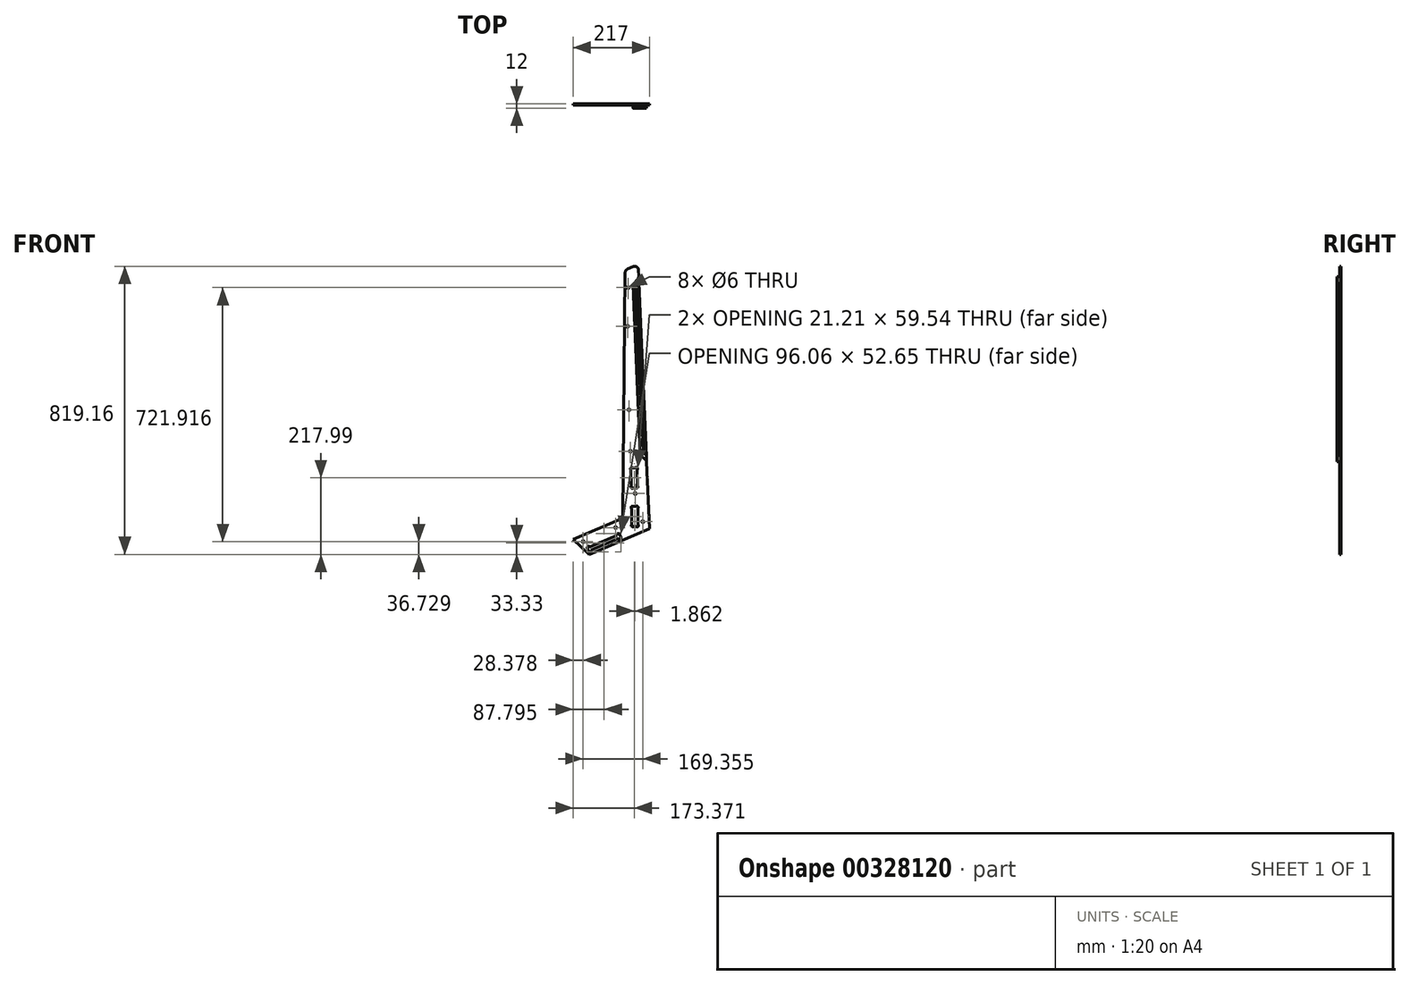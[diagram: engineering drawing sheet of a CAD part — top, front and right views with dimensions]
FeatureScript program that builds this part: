
annotation { "Feature Type Name" : "Feature", "Feature Type Description" : "" }
export const myFeature = defineFeature(function(context is Context, id is Id, definition is map)
    precondition{}
    {
        {
            var Q0;
            Q0=qCreatedBy(makeId("Front.planeOp"),FACE);
            var sketch = newSketch(context, id + "F0", { "sketchPlane" : qUnion([Q0])});
            skArc(sketch, "E0", {"start": v(65.23, -72.8) * mm, "mid": v(65.32, -78.46) * mm, "end": v(70.98, -78.36) * mm});
            skLineSegment(sketch, "E1", {"start": v(70.98, -78.36) * mm, "end": v(77.67, -78.25) * mm});
            skArc(sketch, "E2", {"start": v(77.67, -78.25) * mm, "mid": v(83.32, -78.15) * mm, "end": v(83.23, -72.5) * mm});
            skLineSegment(sketch, "E3", {"start": v(83.23, -72.5) * mm, "end": v(82.45, -26.82) * mm});
            skArc(sketch, "E4", {"start": v(82.45, -26.82) * mm, "mid": v(82.36, -21.16) * mm, "end": v(76.7, -21.26) * mm});
            skLineSegment(sketch, "E5", {"start": v(76.7, -21.26) * mm, "end": v(70.02, -21.37) * mm});
            skArc(sketch, "E6", {"start": v(70.02, -21.37) * mm, "mid": v(64.36, -21.47) * mm, "end": v(64.46, -27.12) * mm});
            skLineSegment(sketch, "E7", {"start": v(64.46, -27.12) * mm, "end": v(65.23, -72.8) * mm});
            skLineSegment(sketch, "E8", {"start": v(85.09, -182.48) * mm, "end": v(84.31, -136.8) * mm});
            skArc(sketch, "E9", {"start": v(84.31, -136.8) * mm, "mid": v(84.22, -131.15) * mm, "end": v(78.56, -131.24) * mm});
            skLineSegment(sketch, "E10", {"start": v(78.56, -131.24) * mm, "end": v(71.88, -131.35) * mm});
            skArc(sketch, "E11", {"start": v(71.88, -131.35) * mm, "mid": v(66.22, -131.45) * mm, "end": v(66.32, -137.1) * mm});
            skLineSegment(sketch, "E12", {"start": v(66.32, -137.1) * mm, "end": v(67.09, -182.79) * mm});
            skArc(sketch, "E13", {"start": v(67.09, -182.79) * mm, "mid": v(67.19, -188.44) * mm, "end": v(72.84, -188.35) * mm});
            skLineSegment(sketch, "E14", {"start": v(72.84, -188.35) * mm, "end": v(79.53, -188.23) * mm});
            skArc(sketch, "E15", {"start": v(79.53, -188.23) * mm, "mid": v(85.18, -188.14) * mm, "end": v(85.09, -182.48) * mm});
            skArc(sketch, "E16", {"start": v(-52.1, -246.94) * mm, "mid": v(-57.35, -244.85) * mm, "end": v(-59.44, -250.1) * mm});
            skLineSegment(sketch, "E17", {"start": v(-59.44, -250.1) * mm, "end": v(-55.88, -258.37) * mm});
            skArc(sketch, "E18", {"start": v(-55.88, -258.37) * mm, "mid": v(-50.62, -260.47) * mm, "end": v(-48.53, -255.21) * mm});
            skLineSegment(sketch, "E19", {"start": v(-48.53, -255.21) * mm, "end": v(28.62, -222) * mm});
            skArc(sketch, "E20", {"start": v(28.62, -222) * mm, "mid": v(33.88, -224.09) * mm, "end": v(35.97, -218.83) * mm});
            skLineSegment(sketch, "E21", {"start": v(35.97, -218.83) * mm, "end": v(32.41, -210.57) * mm});
            skArc(sketch, "E22", {"start": v(32.41, -210.57) * mm, "mid": v(27.15, -208.47) * mm, "end": v(25.06, -213.73) * mm});
            skLineSegment(sketch, "E23", {"start": v(25.06, -213.73) * mm, "end": v(-52.1, -246.94) * mm});
            skArc(sketch, "E24", {"start": v(41.94, -161.76) * mm, "mid": v(41.27, -163.94) * mm, "end": v(39.52, -165.4) * mm});
            skLineSegment(sketch, "E25", {"start": v(39.52, -165.4) * mm, "end": v(-99.53, -225.26) * mm});
            skLineSegment(sketch, "E26", {"start": v(-99.53, -225.26) * mm, "end": v(-53.74, -267.8) * mm});
            skLineSegment(sketch, "E27", {"start": v(-53.74, -267.8) * mm, "end": v(41.34, -226.86) * mm});
            skLineSegment(sketch, "E28", {"start": v(41.34, -226.86) * mm, "end": v(117.47, -194.09) * mm});
            skLineSegment(sketch, "E29", {"start": v(117.47, -194.09) * mm, "end": v(85.73, 541.79) * mm});
            skArc(sketch, "E30", {"start": v(85.73, 541.79) * mm, "mid": v(81.05, 549.82) * mm, "end": v(71.78, 550.54) * mm});
            skLineSegment(sketch, "E31", {"start": v(71.78, 550.54) * mm, "end": v(54.43, 543.07) * mm});
            skArc(sketch, "E32", {"start": v(54.43, 543.07) * mm, "mid": v(50.05, 539.42) * mm, "end": v(48.38, 533.98) * mm});
            skLineSegment(sketch, "E33", {"start": v(48.38, 533.98) * mm, "end": v(41.94, -161.76) * mm});
            skCircle(sketch, "E34", {"center": v(56.39, 490.84) * mm, "radius": 3 * mm});
            skCircle(sketch, "E35", {"center": v(55.37, 380.85) * mm, "radius": 3 * mm});
            skCircle(sketch, "E36", {"center": v(-71.15, -231.07) * mm, "radius": 3 * mm});
            skCircle(sketch, "E37", {"center": v(76.63, -94.57) * mm, "radius": 3 * mm});
            skCircle(sketch, "E38", {"center": v(21.3, -191.27) * mm, "radius": 3 * mm});
            skCircle(sketch, "E39", {"center": v(63.23, 25.56) * mm, "radius": 3 * mm});
            skCircle(sketch, "E40", {"center": v(59.35, 143.54) * mm, "radius": 3 * mm});
            skCircle(sketch, "E41", {"center": v(98.2, -174.5) * mm, "radius": 3 * mm});
            skLineSegment(sketch, "E42", {"start": v(96.02, 524.96) * mm, "end": v(118.95, -6.55) * mm});
            skArc(sketch, "E43", {"start": v(118.95, -6.55) * mm, "mid": v(114.38, -11.53) * mm, "end": v(109.4, -6.96) * mm});
            skLineSegment(sketch, "E44", {"start": v(109.4, -6.96) * mm, "end": v(109.28, -4.28) * mm});
            skArc(sketch, "E45", {"start": v(109.28, -4.28) * mm, "mid": v(108.54, -1.25) * mm, "end": v(106.7, 1.27) * mm});
            skLineSegment(sketch, "E46", {"start": v(106.7, 1.27) * mm, "end": v(92.42, 14.37) * mm});
            skArc(sketch, "E47", {"start": v(92.42, 14.37) * mm, "mid": v(91.5, 15.63) * mm, "end": v(91.13, 17.14) * mm});
            skLineSegment(sketch, "E48", {"start": v(91.13, 17.14) * mm, "end": v(70.34, 498.96) * mm});
            skArc(sketch, "E49", {"start": v(70.34, 498.96) * mm, "mid": v(70.58, 500.5) * mm, "end": v(71.4, 501.83) * mm});
            skLineSegment(sketch, "E50", {"start": v(71.4, 501.83) * mm, "end": v(84.49, 516.1) * mm});
            skArc(sketch, "E51", {"start": v(84.49, 516.1) * mm, "mid": v(86.11, 518.78) * mm, "end": v(86.59, 521.86) * mm});
            skLineSegment(sketch, "E52", {"start": v(86.59, 521.86) * mm, "end": v(86.47, 524.54) * mm});
            skArc(sketch, "E53", {"start": v(86.47, 524.54) * mm, "mid": v(91.04, 529.53) * mm, "end": v(96.02, 524.96) * mm});
            skArc(sketch, "E54", {"start": v(99.45, 23.9) * mm, "mid": v(99.82, 22.39) * mm, "end": v(100.74, 21.13) * mm});
            skLineSegment(sketch, "E55", {"start": v(100.74, 21.13) * mm, "end": v(106.05, 16.26) * mm});
            skArc(sketch, "E56", {"start": v(106.05, 16.26) * mm, "mid": v(107.9, 13.74) * mm, "end": v(108.63, 10.7) * mm});
            skLineSegment(sketch, "E57", {"start": v(108.63, 10.7) * mm, "end": v(108.75, 8.02) * mm});
            skArc(sketch, "E58", {"start": v(108.75, 8.02) * mm, "mid": v(113.73, 3.45) * mm, "end": v(118.3, 8.44) * mm});
            skArc(sketch, "E59", {"start": v(96.67, 509.97) * mm, "mid": v(91.69, 514.54) * mm, "end": v(87.12, 509.56) * mm});
            skLineSegment(sketch, "E60", {"start": v(87.12, 509.56) * mm, "end": v(87.23, 506.87) * mm});
            skArc(sketch, "E61", {"start": v(87.23, 506.87) * mm, "mid": v(86.76, 503.79) * mm, "end": v(85.14, 501.12) * mm});
            skLineSegment(sketch, "E62", {"start": v(85.14, 501.12) * mm, "end": v(80.27, 495.82) * mm});
            skArc(sketch, "E63", {"start": v(80.27, 495.82) * mm, "mid": v(79.46, 494.48) * mm, "end": v(79.22, 492.94) * mm});
            skLineSegment(sketch, "E64", {"start": v(79.22, 492.94) * mm, "end": v(99.45, 23.9) * mm});
            skSolve(sketch);
        }
        {
            var Q0;
            {var subQ3=sQuery(id+"F0.wireOp",EDGE,"E45");Q0=makeQuery(id+"F0.imprint","IMPRINT",FACE,{"disambiguationData":[TD([[makeQuery(id+"F0.imprint","IMPRINT",EDGE,{"derivedFrom":subQ3}),-1.0]])]});}
            var Q1;
            Q1=makeQuery(id+"F0.imprint","IMPRINT",FACE,{"disambiguationData":[TD([[makeQuery(id+"F0.imprint","IMPRINT",EDGE,{"derivedFrom":sQuery(id+"F0.wireOp",EDGE,"E54")}),1.0]])]});
            var Q2;
            Q2=makeQuery(id+"F0.imprint","IMPRINT",FACE,{"disambiguationData":[TD([[makeQuery(id+"F0.imprint","IMPRINT",EDGE,{"derivedFrom":sQuery(id+"F0.wireOp",EDGE,"E36")}),-1.0]])]});
            var Q3;
            Q3=makeQuery(id+"F0.imprint","IMPRINT",FACE,{"disambiguationData":[TD([[makeQuery(id+"F0.imprint","IMPRINT",EDGE,{"derivedFrom":sQuery(id+"F0.wireOp",EDGE,"E41")}),-1.0]])]});
            var Q4;
            Q4=makeQuery(id+"F0.imprint","IMPRINT",FACE,{"disambiguationData":[TD([[makeQuery(id+"F0.imprint","IMPRINT",EDGE,{"derivedFrom":sQuery(id+"F0.wireOp",EDGE,"E38")}),-1.0]])]});
            var Q5;
            Q5=makeQuery(id+"F0.imprint","IMPRINT",FACE,{"disambiguationData":[TD([[makeQuery(id+"F0.imprint","IMPRINT",EDGE,{"derivedFrom":sQuery(id+"F0.wireOp",EDGE,"E37")}),-1.0]])]});
            var Q6;
            Q6=makeQuery(id+"F0.imprint","IMPRINT",FACE,{"disambiguationData":[TD([[makeQuery(id+"F0.imprint","IMPRINT",EDGE,{"derivedFrom":sQuery(id+"F0.wireOp",EDGE,"E0")}),-1.0]])]});
            var Q7;
            Q7=makeQuery(id+"F0.imprint","IMPRINT",FACE,{"disambiguationData":[TD([[makeQuery(id+"F0.imprint","IMPRINT",EDGE,{"derivedFrom":sQuery(id+"F0.wireOp",EDGE,"E39")}),-1.0]])]});
            var Q8;
            Q8=makeQuery(id+"F0.imprint","IMPRINT",FACE,{"disambiguationData":[TD([[makeQuery(id+"F0.imprint","IMPRINT",EDGE,{"derivedFrom":sQuery(id+"F0.wireOp",EDGE,"E40")}),-1.0]])]});
            var Q9;
            Q9=makeQuery(id+"F0.imprint","IMPRINT",FACE,{"disambiguationData":[TD([[makeQuery(id+"F0.imprint","IMPRINT",EDGE,{"derivedFrom":sQuery(id+"F0.wireOp",EDGE,"E35")}),-1.0]])]});
            var Q10;
            Q10=makeQuery(id+"F0.imprint","IMPRINT",FACE,{"disambiguationData":[TD([[makeQuery(id+"F0.imprint","IMPRINT",EDGE,{"derivedFrom":sQuery(id+"F0.wireOp",EDGE,"E34")}),-1.0]])]});
            extrude(context, id + "F1", {"entities" : qUnion([Q0, Q1, Q2, Q3, Q4, Q5, Q6, Q7, Q8, Q9, Q10]), "oppositeDirection" : true, "depth" : 18 * mm});
        }
        {
            var Q0;
            Q0=makeQuery(id+"F0.imprint","IMPRINT",FACE,{"disambiguationData":[TD([[makeQuery(id+"F0.imprint","IMPRINT",EDGE,{"derivedFrom":sQuery(id+"F0.wireOp",EDGE,"E40")}),-1.0]])]});
            var Q1;
            Q1=makeQuery(id+"F0.imprint","IMPRINT",FACE,{"disambiguationData":[TD([[makeQuery(id+"F0.imprint","IMPRINT",EDGE,{"derivedFrom":sQuery(id+"F0.wireOp",EDGE,"E39")}),-1.0]])]});
            var Q2;
            Q2=makeQuery(id+"F0.imprint","IMPRINT",FACE,{"disambiguationData":[TD([[makeQuery(id+"F0.imprint","IMPRINT",EDGE,{"derivedFrom":sQuery(id+"F0.wireOp",EDGE,"E35")}),-1.0]])]});
            var Q3;
            Q3=makeQuery(id+"F0.imprint","IMPRINT",FACE,{"disambiguationData":[TD([[makeQuery(id+"F0.imprint","IMPRINT",EDGE,{"derivedFrom":sQuery(id+"F0.wireOp",EDGE,"E34")}),-1.0]])]});
            var Q4;
            Q4=makeQuery(id+"F0.imprint","IMPRINT",FACE,{"disambiguationData":[TD([[makeQuery(id+"F0.imprint","IMPRINT",EDGE,{"derivedFrom":sQuery(id+"F0.wireOp",EDGE,"E38")}),-1.0]])]});
            var Q5;
            Q5=makeQuery(id+"F0.imprint","IMPRINT",FACE,{"disambiguationData":[TD([[makeQuery(id+"F0.imprint","IMPRINT",EDGE,{"derivedFrom":sQuery(id+"F0.wireOp",EDGE,"E41")}),-1.0]])]});
            var Q6;
            Q6=makeQuery(id+"F0.imprint","IMPRINT",FACE,{"disambiguationData":[TD([[makeQuery(id+"F0.imprint","IMPRINT",EDGE,{"derivedFrom":sQuery(id+"F0.wireOp",EDGE,"E37")}),-1.0]])]});
            var Q7;
            Q7=makeQuery(id+"F0.imprint","IMPRINT",FACE,{"disambiguationData":[TD([[makeQuery(id+"F0.imprint","IMPRINT",EDGE,{"derivedFrom":sQuery(id+"F0.wireOp",EDGE,"E36")}),-1.0]])]});
            extrude(context, id + "F2", {"entities" : qUnion([Q0, Q1, Q2, Q3, Q4, Q5, Q6, Q7]), "operationType" : NewBodyOperationType.REMOVE, "oppositeDirection" : true, "depth" : 14 * mm});
        }
        {
            var Q0;
            Q0=makeQuery(id+"F0.imprint","IMPRINT",FACE,{"disambiguationData":[TD([[makeQuery(id+"F0.imprint","IMPRINT",EDGE,{"derivedFrom":sQuery(id+"F0.wireOp",EDGE,"E54")}),1.0]])]});
            extrude(context, id + "F3", {"entities" : qUnion([Q0]), "operationType" : NewBodyOperationType.REMOVE, "oppositeDirection" : true, "depth" : 9 * mm});
        }
        {
            var Q0;
            {var subQ3=sQuery(id+"F0.wireOp",EDGE,"E45");Q0=makeQuery(id+"F0.imprint","IMPRINT",FACE,{"disambiguationData":[TD([[makeQuery(id+"F0.imprint","IMPRINT",EDGE,{"derivedFrom":subQ3}),-1.0]])]});}
            extrude(context, id + "F4", {"entities" : qUnion([Q0]), "operationType" : NewBodyOperationType.REMOVE, "oppositeDirection" : true, "depth" : 6 * mm});
        }
    });
